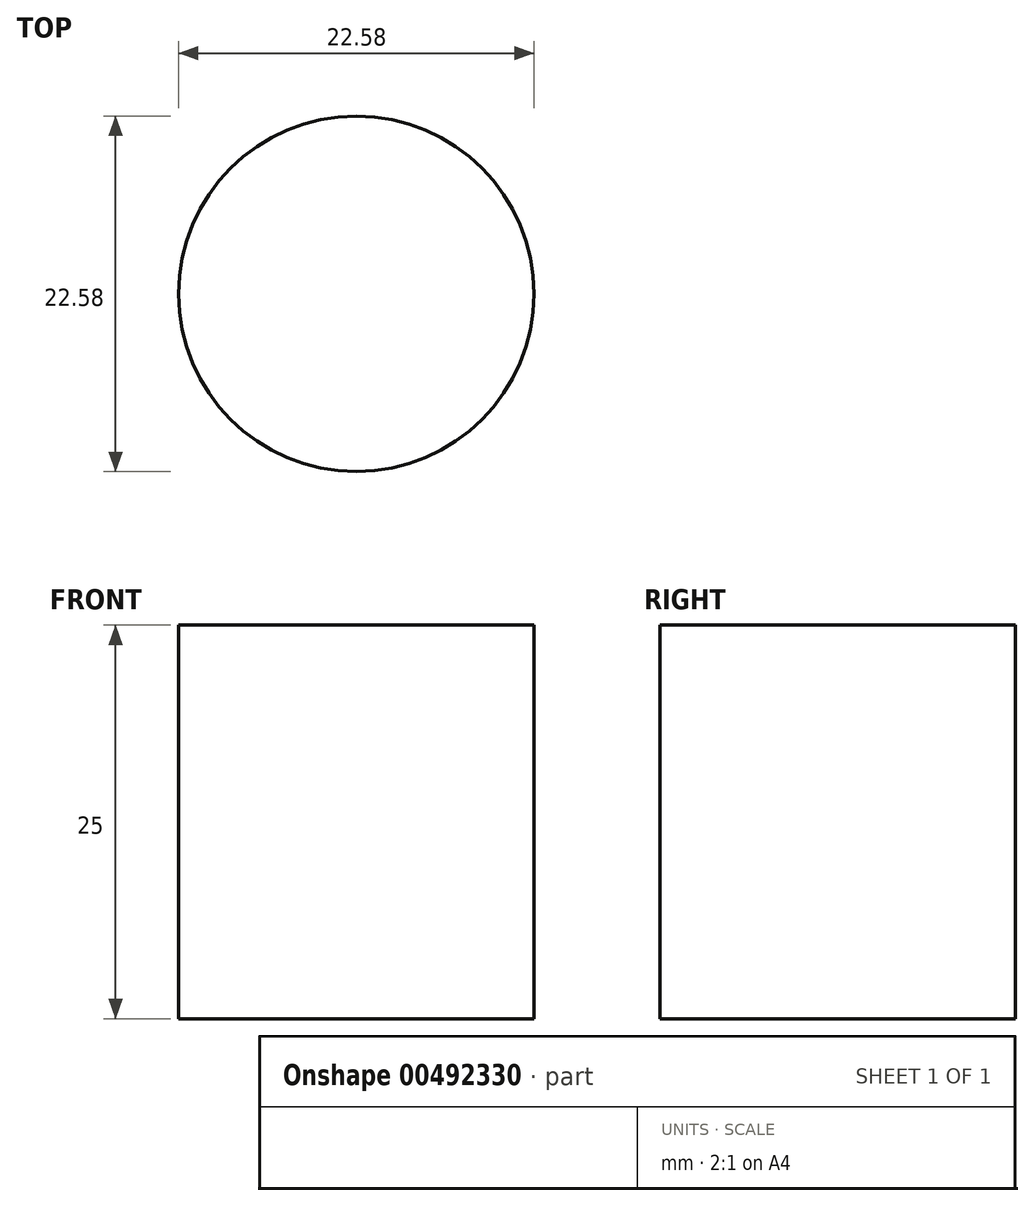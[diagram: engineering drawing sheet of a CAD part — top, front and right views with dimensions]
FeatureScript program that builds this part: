
annotation { "Feature Type Name" : "Feature", "Feature Type Description" : "" }
export const myFeature = defineFeature(function(context is Context, id is Id, definition is map)
    precondition{}
    {
        {
            var Q0;
            Q0=qCreatedBy(makeId("Top.planeOp"),FACE);
            var sketch = newSketch(context, id + "F0", { "sketchPlane" : qUnion([Q0])});
            skCircle(sketch, "E0", {"center": v(0, 0) * mm, "radius": 11.29 * mm});
            skSolve(sketch);
        }
        {
            var Q0;
            Q0=makeQuery(id+"F0.imprint","IMPRINT",FACE,{"disambiguationData":[TD([[makeQuery(id+"F0.imprint","IMPRINT",EDGE,{"derivedFrom":sQuery(id+"F0.wireOp",EDGE,"E0")}),1.0]])]});
            extrude(context, id + "F1", {"entities" : qUnion([Q0]), "depth" : 25 * mm});
        }
    });
